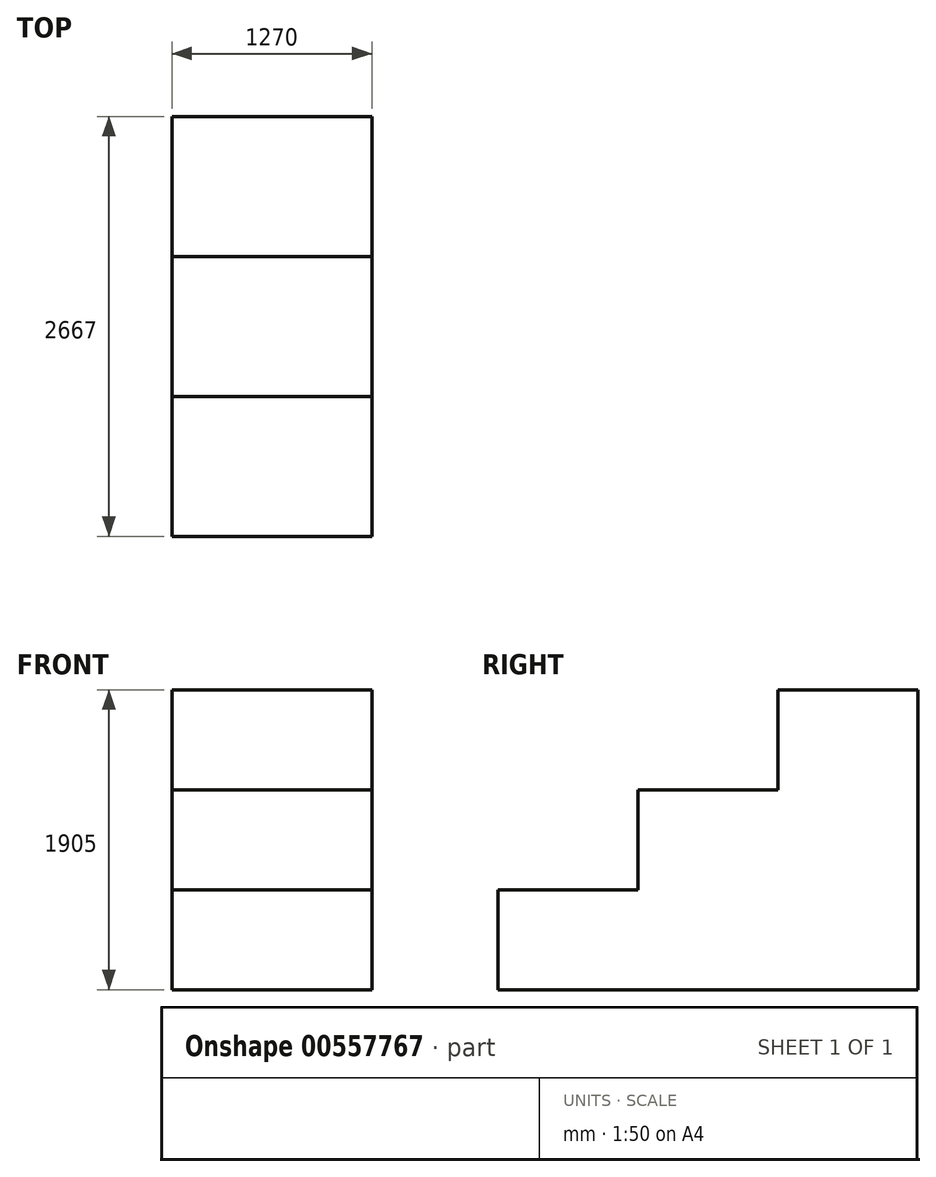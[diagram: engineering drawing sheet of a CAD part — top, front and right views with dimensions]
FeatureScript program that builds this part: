
annotation { "Feature Type Name" : "Feature", "Feature Type Description" : "" }
export const myFeature = defineFeature(function(context is Context, id is Id, definition is map)
    precondition{}
    {
        {
            var Q0;
            Q0=qCreatedBy(makeId("Right.planeOp"),FACE);
            var sketch = newSketch(context, id + "F0", { "sketchPlane" : qUnion([Q0])});
            skLineSegment(sketch, "E0", {"start": v(-63.26, -59.8) * mm, "end": v(2603.74, -59.8) * mm});
            skLineSegment(sketch, "E1", {"start": v(2603.74, -59.8) * mm, "end": v(2603.74, 1845.2) * mm});
            skLineSegment(sketch, "E2", {"start": v(2603.74, 1845.2) * mm, "end": v(1714.74, 1845.2) * mm});
            skLineSegment(sketch, "E3", {"start": v(1714.74, 1845.2) * mm, "end": v(1714.74, 1210.2) * mm});
            skLineSegment(sketch, "E4", {"start": v(1714.74, 1210.2) * mm, "end": v(825.74, 1210.2) * mm});
            skLineSegment(sketch, "E5", {"start": v(825.74, 1210.2) * mm, "end": v(825.74, 575.2) * mm});
            skLineSegment(sketch, "E6", {"start": v(825.74, 575.2) * mm, "end": v(-63.26, 575.2) * mm});
            skLineSegment(sketch, "E7", {"start": v(-63.26, 575.2) * mm, "end": v(-63.26, -59.8) * mm});
            skSolve(sketch);
        }
        {
            var Q0;
            Q0=makeQuery(id+"F0.imprint","IMPRINT",FACE,{"disambiguationData":[TD([[makeQuery(id+"F0.imprint","IMPRINT",EDGE,{"derivedFrom":sQuery(id+"F0.wireOp",EDGE,"E0")}),1.0]])]});
            extrude(context, id + "F1", {"entities" : qUnion([Q0]), "oppositeDirection" : true, "depth" : 1270 * mm, "offsetDistance" : 25.4 * mm});
        }
    });
